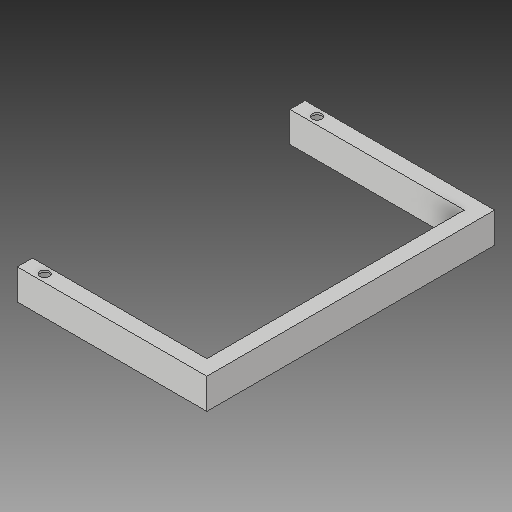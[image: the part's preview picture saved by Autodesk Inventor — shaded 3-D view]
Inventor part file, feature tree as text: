
AUTODESK INVENTOR PART (.ipt)
format: ipt  version: 2019 (Build 230136000, 136)  size: 125,952 bytes
history: native  units: in
note: dims shown in document units (in); Inventor stores cm internally (conversion verified against a paired STEP export)
features: sketch x3, plane x1, sweep x1, extrude x1, mirror x1
ambient origin geometry x8: Origin, YZ Plane, XZ Plane, XY Plane, X Axis, Y Axis, Z Axis, Center Point
bodies: Solid1 (feature_tree)
feature tree (7):
  sketch  "Sketch1"  dims[d0=12.0in d1=9.0in]
  plane  "Work Plane1"
  sweep  "Sweep1"
  extrude  "Extrusion1"  Depth=1.0in
  mirror  "Mirror1"
  sketch  "Sketch2"  dims[d2=-12.0in d3=1.0in]
  sketch  "Sketch3"  dims[d4=2.0in d5=0.125in d6=0.125in d7=0.0in d8=0.0in d9=0.625in d10=1.295in d11=1.0in d12=0.0in]
